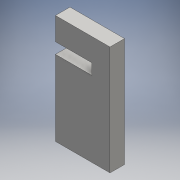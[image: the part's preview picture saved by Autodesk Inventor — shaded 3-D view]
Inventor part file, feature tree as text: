
AUTODESK INVENTOR PART (.ipt)
format: ipt  version: 2016 (Build 200138000, 138)  size: 95,232 bytes
history: native  units: mm
features: extrude x1, sketch x1
ambient origin geometry x8: Origin, YZ Plane, XZ Plane, XY Plane, X Axis, Y Axis, Z Axis, Center Point
bodies: Solid1 (feature_tree)
feature tree (2):
  extrude  "Extrusion1"  Depth=30.0mm
  sketch  "Sketch1"  dims[d0=15.0mm d1=30.0mm d2=10.0mm d3=20.75mm d4=4.0mm d5=0.0mm d6=3.0mm]
